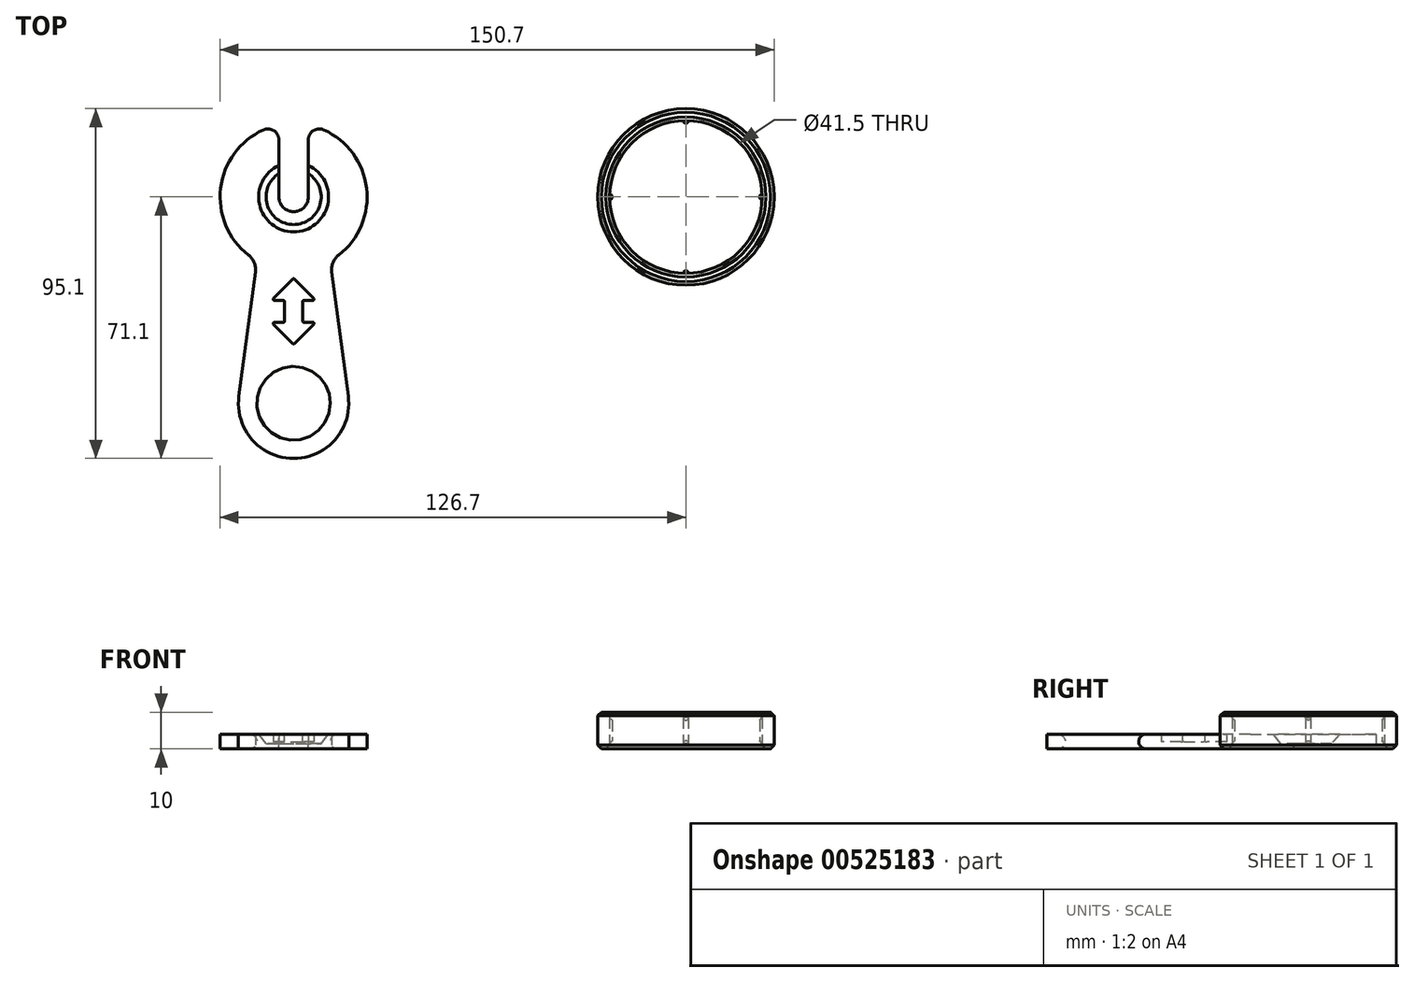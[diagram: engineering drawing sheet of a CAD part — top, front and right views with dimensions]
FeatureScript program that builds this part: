
annotation { "Feature Type Name" : "Feature", "Feature Type Description" : "" }
export const myFeature = defineFeature(function(context is Context, id is Id, definition is map)
    precondition{}
    {
        {
            assignVariable(context, id + "F0", {"name" : "SPACER_DEPTH", "anyValue" : 10 * mm});
        }
        {
            var Q0;
            Q0=qCreatedBy(makeId("Top.planeOp"),FACE);
            var sketch = newSketch(context, id + "F1", { "sketchPlane" : qUnion([Q0])});
            skCircle(sketch, "E0", {"center": v(0, 0) * mm, "radius": 20.75 * mm});
            skCircle(sketch, "E1.0", {"center": v(0, 0) * mm, "radius": 24 * mm});
            skSolve(sketch);
        }
        {
            var Q0;
            Q0=makeQuery(id+"F1.imprint","IMPRINT",FACE,{"disambiguationData":[TD([[makeQuery(id+"F1.imprint","IMPRINT",EDGE,{"derivedFrom":sQuery(id+"F1.wireOp",EDGE,"E0")}),-1.0]])]});
            extrude(context, id + "F2", {"entities" : qUnion([Q0]), "depth" : getVariable(context, 'SPACER_DEPTH'), "offsetDistance" : 25 * mm});
        }
        {
            var Q0;
            Q0=makeQuery(id+"F2.opExtrude","CAP_EDGE",EDGE,{"disambiguationData":[OSD([sQuery(id+"F1.wireOp",EDGE,"E0")])],"isStart":false});
            var Q1;
            Q1=makeQuery(id+"F2.opExtrude","CAP_EDGE",EDGE,{"disambiguationData":[OSD([sQuery(id+"F1.wireOp",EDGE,"E0")])],"isStart":true});
            var Q2;
            Q2=makeQuery(id+"F2.opExtrude","CAP_EDGE",EDGE,{"disambiguationData":[OSD([sQuery(id+"F1.wireOp",EDGE,"E1.0")])],"isStart":false});
            var Q3;
            Q3=makeQuery(id+"F2.opExtrude","CAP_EDGE",EDGE,{"disambiguationData":[OSD([sQuery(id+"F1.wireOp",EDGE,"E1.0")])],"isStart":true});
            chamfer(context, id + "F3", {"entities" : qUnion([Q0, Q1, Q2, Q3]), "width" : 1 * mm, "tangentPropagation" : true});
        }
        {
            var Q0;
            Q0=qCreatedBy(makeId("Top.planeOp"),FACE);
            cPlane(context, id + "F4", {"entities" : qUnion([Q0]), "cplaneType" : CPlaneType.OFFSET, "offset" : getVariable(context, 'SPACER_DEPTH') / 2, "width" : 150 * mm, "height" : 150 * mm});
        }
        {
            var Q0;
            Q0=qCreatedBy(id+"F4.planeOp",FACE);
            var sketch = newSketch(context, id + "F5", { "sketchPlane" : qUnion([Q0])});
            skCircle(sketch, "E2.0", {"center": v(0, 0) * mm, "radius": 20.75 * mm, "construction": true});
            skCircle(sketch, "E3", {"center": v(-20.75, 0) * mm, "radius": 0.7 * mm});
            skCircle(sketch, "E4.1.0", {"center": v(0, -20.75) * mm, "radius": 0.7 * mm});
            skCircle(sketch, "E4.2.0", {"center": v(20.75, 0) * mm, "radius": 0.7 * mm});
            skCircle(sketch, "E4.3.0", {"center": v(0, 20.75) * mm, "radius": 0.7 * mm});
            skSolve(sketch);
        }
        {
            var Q0;
            Q0 = qSketchRegion(id + "F5", true);
            extrude(context, id + "F6", {"entities" : qUnion([Q0]), "operationType" : NewBodyOperationType.ADD, "endBound" : BoundingType.SYMMETRIC, "depth" : getVariable(context, 'SPACER_DEPTH') / 2, "offsetDistance" : 25 * mm});
        }
        {
            var Q0;
            Q0=makeQuery(id+"F6.boolean.opBoolean","INTERSECT",EDGE,{"derivedFrom":[makeQuery(id+"F2.opExtrude","SWEPT_FACE",FACE,{"disambiguationData":[OSD([sQuery(id+"F1.wireOp",EDGE,"E0")])]}),makeQuery(id+"F6.opExtrude","CAP_FACE",FACE,{"disambiguationData":[OSD([sQuery(id+"F5.wireOp",EDGE,"E4.3.0")])],"isStart":false})]});
            var Q1;
            Q1=makeQuery(id+"F6.boolean.opBoolean","INTERSECT",EDGE,{"derivedFrom":[makeQuery(id+"F2.opExtrude","SWEPT_FACE",FACE,{"disambiguationData":[OSD([sQuery(id+"F1.wireOp",EDGE,"E0")])]}),makeQuery(id+"F6.opExtrude","CAP_FACE",FACE,{"disambiguationData":[OSD([sQuery(id+"F5.wireOp",EDGE,"E3")])],"isStart":false})]});
            var Q2;
            Q2=makeQuery(id+"F6.boolean.opBoolean","INTERSECT",EDGE,{"derivedFrom":[makeQuery(id+"F2.opExtrude","SWEPT_FACE",FACE,{"disambiguationData":[OSD([sQuery(id+"F1.wireOp",EDGE,"E0")])]}),makeQuery(id+"F6.opExtrude","CAP_FACE",FACE,{"disambiguationData":[OSD([sQuery(id+"F5.wireOp",EDGE,"E4.2.0")])],"isStart":false})]});
            var Q3;
            Q3=makeQuery(id+"F6.boolean.opBoolean","INTERSECT",EDGE,{"derivedFrom":[makeQuery(id+"F2.opExtrude","SWEPT_FACE",FACE,{"disambiguationData":[OSD([sQuery(id+"F1.wireOp",EDGE,"E0")])]}),makeQuery(id+"F6.opExtrude","CAP_FACE",FACE,{"disambiguationData":[OSD([sQuery(id+"F5.wireOp",EDGE,"E4.1.0")])],"isStart":false})]});
            var Q4;
            Q4=makeQuery(id+"F6.boolean.opBoolean","INTERSECT",EDGE,{"derivedFrom":[makeQuery(id+"F2.opExtrude","SWEPT_FACE",FACE,{"disambiguationData":[OSD([sQuery(id+"F1.wireOp",EDGE,"E0")])]}),makeQuery(id+"F6.opExtrude","CAP_FACE",FACE,{"disambiguationData":[OSD([sQuery(id+"F5.wireOp",EDGE,"E4.3.0")])],"isStart":true})]});
            var Q5;
            Q5=makeQuery(id+"F6.boolean.opBoolean","INTERSECT",EDGE,{"derivedFrom":[makeQuery(id+"F2.opExtrude","SWEPT_FACE",FACE,{"disambiguationData":[OSD([sQuery(id+"F1.wireOp",EDGE,"E0")])]}),makeQuery(id+"F6.opExtrude","CAP_FACE",FACE,{"disambiguationData":[OSD([sQuery(id+"F5.wireOp",EDGE,"E4.2.0")])],"isStart":true})]});
            var Q6;
            Q6=makeQuery(id+"F6.boolean.opBoolean","INTERSECT",EDGE,{"derivedFrom":[makeQuery(id+"F2.opExtrude","SWEPT_FACE",FACE,{"disambiguationData":[OSD([sQuery(id+"F1.wireOp",EDGE,"E0")])]}),makeQuery(id+"F6.opExtrude","CAP_FACE",FACE,{"disambiguationData":[OSD([sQuery(id+"F5.wireOp",EDGE,"E4.1.0")])],"isStart":true})]});
            var Q7;
            Q7=makeQuery(id+"F6.boolean.opBoolean","INTERSECT",EDGE,{"derivedFrom":[makeQuery(id+"F2.opExtrude","SWEPT_FACE",FACE,{"disambiguationData":[OSD([sQuery(id+"F1.wireOp",EDGE,"E0")])]}),makeQuery(id+"F6.opExtrude","CAP_FACE",FACE,{"disambiguationData":[OSD([sQuery(id+"F5.wireOp",EDGE,"E3")])],"isStart":true})]});
            chamfer(context, id + "F7", {"entities" : qUnion([Q0, Q1, Q2, Q3, Q4, Q5, Q6, Q7]), "width" : 1 * mm, "tangentPropagation" : true});
        }
        {
            var Q0;
            Q0=qCreatedBy(makeId("Top.planeOp"),FACE);
            var sketch = newSketch(context, id + "F8", { "sketchPlane" : qUnion([Q0])});
            skCircle(sketch, "E5", {"center": v(-106.7, 0) * mm, "radius": 4 * mm});
            skCircle(sketch, "E6", {"center": v(-106.7, 0) * mm, "radius": 20 * mm});
            skCircle(sketch, "E7", {"center": v(-106.7, -56.1) * mm, "radius": 15 * mm});
            skLineSegment(sketch, "E8", {"start": v(-106.7, 31.77) * mm, "end": v(-106.7, -83.91) * mm, "construction": true});
            skLineSegment(sketch, "E9", {"start": v(-116.7, -17.32) * mm, "end": v(-121.57, -54.13) * mm});
            skLineSegment(sketch, "E10", {"start": v(-96.7, -17.32) * mm, "end": v(-91.83, -54.13) * mm});
            skCircle(sketch, "E11.0", {"center": v(-106.7, -56.1) * mm, "radius": 10 * mm});
            skSolve(sketch);
        }
        {
            var Q0;
            {var subQ0=sQuery(id+"F8.wireOp",EDGE,"tMZcsfvI-P9a6-IfvE-EsAQ-RMbjLVvdxzLP");var subQ1=sQuery(id+"F8.wireOp",EDGE,"E5");var subQ2=makeQuery(id+"F8.imprint","INTERSECT",VERTEX,{"disambiguationData":[OD(0.0)],"derivedFrom":[subQ1,subQ0]});Q0=makeQuery(id+"F8.imprint","IMPRINT",FACE,{"disambiguationData":[TD([[makeQuery(id+"F8.imprint","IMPRINT",EDGE,{"disambiguationData":[TD([[subQ2,-1.0]])],"derivedFrom":subQ1}),-1.0]])]});}
            var Q1;
            {var subQ0=sQuery(id+"F8.wireOp",EDGE,"tMZcsfvI-P9a6-IfvE-EsAQ-RMbjLVvdxzLP");var subQ1=sQuery(id+"F8.wireOp",EDGE,"E5");var subQ2=makeQuery(id+"F8.imprint","INTERSECT",VERTEX,{"disambiguationData":[OD(0.0)],"derivedFrom":[subQ1,subQ0]});Q1=makeQuery(id+"F8.imprint","IMPRINT",FACE,{"disambiguationData":[TD([[makeQuery(id+"F8.imprint","IMPRINT",EDGE,{"disambiguationData":[TD([[subQ2,1.0]])],"derivedFrom":subQ1}),-1.0]])]});}
            var Q2;
            {var subQ0=sQuery(id+"F8.wireOp",EDGE,"d99b7d63-3b80-4857-949c-220825ab7e3a.1.0");var subQ1=sQuery(id+"F8.wireOp",EDGE,"E5");var subQ2=makeQuery(id+"F8.imprint","INTERSECT",VERTEX,{"disambiguationData":[OD(0.0)],"derivedFrom":[subQ1,subQ0]});Q2=makeQuery(id+"F8.imprint","IMPRINT",FACE,{"disambiguationData":[TD([[makeQuery(id+"F8.imprint","IMPRINT",EDGE,{"disambiguationData":[TD([[subQ2,1.0]])],"derivedFrom":subQ1}),-1.0]])]});}
            var Q3;
            {var subQ0=sQuery(id+"F8.wireOp",EDGE,"tMZcsfvI-P9a6-IfvE-EsAQ-RMbjLVvdxzLP");var subQ1=sQuery(id+"F8.wireOp",EDGE,"E5");var subQ2=makeQuery(id+"F8.imprint","INTERSECT",VERTEX,{"disambiguationData":[OD(1.0)],"derivedFrom":[subQ1,subQ0]});Q3=makeQuery(id+"F8.imprint","IMPRINT",FACE,{"disambiguationData":[TD([[makeQuery(id+"F8.imprint","IMPRINT",EDGE,{"disambiguationData":[TD([[subQ2,-1.0]])],"derivedFrom":subQ1}),-1.0]])]});}
            var Q4;
            {var subQ0=sQuery(id+"F8.wireOp",EDGE,"d99b7d63-3b80-4857-949c-220825ab7e3a.1.0");var subQ1=sQuery(id+"F8.wireOp",EDGE,"E5");var subQ2=makeQuery(id+"F8.imprint","INTERSECT",VERTEX,{"disambiguationData":[OD(1.0)],"derivedFrom":[subQ1,subQ0]});Q4=makeQuery(id+"F8.imprint","IMPRINT",FACE,{"disambiguationData":[TD([[makeQuery(id+"F8.imprint","IMPRINT",EDGE,{"disambiguationData":[TD([[subQ2,-1.0]])],"derivedFrom":subQ1}),-1.0]])]});}
            var Q5;
            {var subQ0=sQuery(id+"F8.wireOp",EDGE,"d99b7d63-3b80-4857-949c-220825ab7e3a.2.0");var subQ1=sQuery(id+"F8.wireOp",EDGE,"E5");var subQ2=makeQuery(id+"F8.imprint","INTERSECT",VERTEX,{"disambiguationData":[OD(0.0)],"derivedFrom":[subQ1,subQ0]});Q5=makeQuery(id+"F8.imprint","IMPRINT",FACE,{"disambiguationData":[TD([[makeQuery(id+"F8.imprint","IMPRINT",EDGE,{"disambiguationData":[TD([[subQ2,-1.0]])],"derivedFrom":subQ1}),-1.0]])]});}
            var Q6;
            {var subQ0=sQuery(id+"F8.wireOp",EDGE,"tMZcsfvI-P9a6-IfvE-EsAQ-RMbjLVvdxzLP");var subQ2=sQuery(id+"F8.wireOp",EDGE,"E6");var subQ3=makeQuery(id+"F8.imprint","INTERSECT",VERTEX,{"disambiguationData":[OD(0.0)],"derivedFrom":[subQ2,subQ0]});Q6=makeQuery(id+"F8.imprint","IMPRINT",FACE,{"disambiguationData":[TD([[makeQuery(id+"F8.imprint","IMPRINT",EDGE,{"disambiguationData":[TD([[subQ3,1.0]])],"derivedFrom":subQ2}),-1.0]])]});}
            var Q7;
            {var subQ3=sQuery(id+"F8.wireOp",EDGE,"Im5QKdEk-1Ov4-L05K-2sT1-LfVvJZR5fO0I");Q7=makeQuery(id+"F8.imprint","IMPRINT",FACE,{"disambiguationData":[TD([[makeQuery(id+"F8.imprint","IMPRINT",EDGE,{"derivedFrom":subQ3}),-1.0]])]});}
            var Q8;
            {var subQ3=sQuery(id+"F8.wireOp",EDGE,"e6c83034-2231-4307-ba1c-9a527880b54f0.MirrorCS");Q8=makeQuery(id+"F8.imprint","IMPRINT",FACE,{"disambiguationData":[TD([[makeQuery(id+"F8.imprint","IMPRINT",EDGE,{"derivedFrom":subQ3}),1.0]])]});}
            var Q9;
            {var subQ3=sQuery(id+"F8.wireOp",EDGE,"7b8f1f18-21e0-4d82-9494-f1d715cf9ae4.2.0");Q9=makeQuery(id+"F8.imprint","IMPRINT",FACE,{"disambiguationData":[TD([[makeQuery(id+"F8.imprint","IMPRINT",EDGE,{"derivedFrom":subQ3}),-1.0]])]});}
            var Q10;
            {var subQ0=sQuery(id+"F8.wireOp",EDGE,"tMZcsfvI-P9a6-IfvE-EsAQ-RMbjLVvdxzLP");var subQ6=sQuery(id+"F8.wireOp",EDGE,"E6");var subQ7=makeQuery(id+"F8.imprint","INTERSECT",VERTEX,{"disambiguationData":[OD(1.0)],"derivedFrom":[subQ6,subQ0]});Q10=makeQuery(id+"F8.imprint","IMPRINT",FACE,{"disambiguationData":[TD([[makeQuery(id+"F8.imprint","IMPRINT",EDGE,{"disambiguationData":[TD([[subQ7,-1.0]])],"derivedFrom":subQ6}),-1.0]])]});}
            var Q11;
            {var subQ3=sQuery(id+"F8.wireOp",EDGE,"92c590d0-b01e-4f62-b96a-7e57a4e76e70.2.0");Q11=makeQuery(id+"F8.imprint","IMPRINT",FACE,{"disambiguationData":[TD([[makeQuery(id+"F8.imprint","IMPRINT",EDGE,{"derivedFrom":subQ3}),1.0]])]});}
            var Q12;
            {var subQ3=sQuery(id+"F8.wireOp",EDGE,"7b8f1f18-21e0-4d82-9494-f1d715cf9ae4.1.0");Q12=makeQuery(id+"F8.imprint","IMPRINT",FACE,{"disambiguationData":[TD([[makeQuery(id+"F8.imprint","IMPRINT",EDGE,{"derivedFrom":subQ3}),-1.0]])]});}
            var Q13;
            {var subQ4=sQuery(id+"F8.wireOp",EDGE,"d99b7d63-3b80-4857-949c-220825ab7e3a.2.0");var subQ6=sQuery(id+"F8.wireOp",EDGE,"E6");var subQ8=makeQuery(id+"F8.imprint","INTERSECT",VERTEX,{"disambiguationData":[OD(0.0)],"derivedFrom":[subQ6,subQ4]});Q13=makeQuery(id+"F8.imprint","IMPRINT",FACE,{"disambiguationData":[TD([[makeQuery(id+"F8.imprint","IMPRINT",EDGE,{"disambiguationData":[TD([[subQ8,-1.0]])],"derivedFrom":subQ6}),-1.0]])]});}
            var Q14;
            {var subQ3=sQuery(id+"F8.wireOp",EDGE,"92c590d0-b01e-4f62-b96a-7e57a4e76e70.1.0");Q14=makeQuery(id+"F8.imprint","IMPRINT",FACE,{"disambiguationData":[TD([[makeQuery(id+"F8.imprint","IMPRINT",EDGE,{"derivedFrom":subQ3}),1.0]])]});}
            var Q15;
            Q15=makeQuery(id+"F8.imprint","IMPRINT",FACE,{"disambiguationData":[TD([[makeQuery(id+"F8.imprint","IMPRINT",EDGE,{"derivedFrom":sQuery(id+"F8.wireOp",EDGE,"E11.0")}),-1.0]])]});
            extrude(context, id + "F9", {"entities" : qUnion([Q0, Q1, Q2, Q3, Q4, Q5, Q6, Q7, Q8, Q9, Q10, Q11, Q12, Q13, Q14, Q15]), "depth" : 4 * mm, "offsetDistance" : 25 * mm});
        }
        {
            var Q0;
            Q0=makeQuery(id+"F9.opExtrude","CAP_FACE",FACE,{"disambiguationData":[OSD([sQuery(id+"F8.wireOp",EDGE,"E5"),sQuery(id+"F8.wireOp",EDGE,"E6"),sQuery(id+"F8.wireOp",EDGE,"JQelNSBS-weLF-Z4lI-uK8G-V99NbtTbeSVU"),sQuery(id+"F8.wireOp",EDGE,"tMZcsfvI-P9a6-IfvE-EsAQ-RMbjLVvdxzLP"),sQuery(id+"F8.wireOp",EDGE,"d99b7d63-3b80-4857-949c-220825ab7e3a.1.0"),sQuery(id+"F8.wireOp",EDGE,"d99b7d63-3b80-4857-949c-220825ab7e3a.2.0"),sQuery(id+"F8.wireOp",EDGE,"Im5QKdEk-1Ov4-L05K-2sT1-LfVvJZR5fO0I"),sQuery(id+"F8.wireOp",EDGE,"7b8f1f18-21e0-4d82-9494-f1d715cf9ae4.1.0"),sQuery(id+"F8.wireOp",EDGE,"7b8f1f18-21e0-4d82-9494-f1d715cf9ae4.2.0"),sQuery(id+"F8.wireOp",EDGE,"e6c83034-2231-4307-ba1c-9a527880b54f0.MirrorCS"),sQuery(id+"F8.wireOp",EDGE,"92c590d0-b01e-4f62-b96a-7e57a4e76e70.1.0"),sQuery(id+"F8.wireOp",EDGE,"92c590d0-b01e-4f62-b96a-7e57a4e76e70.2.0")])],"isStart":false});
            var sketch = newSketch(context, id + "F10", { "sketchPlane" : qUnion([Q0])});
            skCircle(sketch, "E12.0", {"center": v(-106.7, 0) * mm, "radius": 4 * mm, "construction": true});
            skCircle(sketch, "E13", {"center": v(-106.7, 0) * mm, "radius": 9.5 * mm});
            skSolve(sketch);
        }
        {
            var Q0;
            Q0=makeQuery(id+"F10.imprint","IMPRINT",FACE,{"disambiguationData":[TD([[makeQuery(id+"F10.imprint","IMPRINT",EDGE,{"derivedFrom":sQuery(id+"F10.wireOp",EDGE,"E13")}),1.0]])]});
            extrude(context, id + "F11", {"entities" : qUnion([Q0]), "operationType" : NewBodyOperationType.REMOVE, "oppositeDirection" : true, "depth" : 2.5 * mm, "offsetDistance" : 25 * mm});
        }
        {
            var Q0;
            Q0=makeQuery(id+"F11.boolean.opBoolean","COPY",EDGE,{"derivedFrom":makeQuery(id+"F11.opExtrude","CAP_EDGE",EDGE,{"disambiguationData":[OSD([sQuery(id+"F10.wireOp",EDGE,"E13")])],"isStart":false})});
            chamfer(context, id + "F12", {"entities" : qUnion([Q0]), "chamferType" : ChamferType.TWO_OFFSETS, "width1" : 2 * mm, "oppositeDirection" : false, "width2" : 2.5 * mm, "tangentPropagation" : true});
        }
        {
            var Q0;
            Q0=makeQuery(id+"F9.opExtrude","CAP_FACE",FACE,{"disambiguationData":[OSD([sQuery(id+"F8.wireOp",EDGE,"E5"),sQuery(id+"F8.wireOp",EDGE,"E6"),sQuery(id+"F8.wireOp",EDGE,"E7"),sQuery(id+"F8.wireOp",EDGE,"E9"),sQuery(id+"F8.wireOp",EDGE,"E10"),sQuery(id+"F8.wireOp",EDGE,"E11.0")])],"isStart":false});
            var sketch = newSketch(context, id + "F13", { "sketchPlane" : qUnion([Q0])});
            skLineSegment(sketch, "E14.0", {"start": v(-106.7, 31.77) * mm, "end": v(-106.7, -83.91) * mm, "construction": true});
            skCircle(sketch, "E15.0", {"center": v(-106.7, 0) * mm, "radius": 4 * mm});
            skLineSegment(sketch, "E16", {"start": v(-110.7, 0) * mm, "end": v(-110.7, 21) * mm});
            skLineSegment(sketch, "E17", {"start": v(-102.7, 0) * mm, "end": v(-102.7, 21) * mm});
            skPoint(sketch, "E18", {"position": v(-106.7, 20) * mm});
            skLineSegment(sketch, "E19", {"start": v(-110.7, 21) * mm, "end": v(-102.7, 21) * mm});
            skSolve(sketch);
        }
        {
            var Q0;
            {var subQ0=sQuery(id+"F13.wireOp",EDGE,"E19");Q0=makeQuery(id+"F13.imprint","IMPRINT",FACE,{"disambiguationData":[TD([[makeQuery(id+"F13.imprint","IMPRINT",EDGE,{"derivedFrom":subQ0}),-1.0]])]});}
            var Q1;
            {var subQ0=sQuery(id+"F13.wireOp",EDGE,"E16");var subQ1=sQuery(id+"F8.wireOp",EDGE,"E6");var subQ2=makeQuery(id+"F9.opExtrude","CAP_EDGE",EDGE,{"disambiguationData":[OSD([subQ1])],"isStart":false});var subQ3=makeQuery(id+"F13.imprint","INTERSECT",VERTEX,{"derivedFrom":[subQ2,subQ0]});Q1=makeQuery(id+"F13.imprint","IMPRINT",FACE,{"disambiguationData":[TD([[makeQuery(id+"F13.imprint","IMPRINT",EDGE,{"disambiguationData":[TD([[subQ3,1.0]])],"derivedFrom":subQ2}),1.0]])]});}
            var Q2;
            {var subQ0=sQuery(id+"F13.wireOp",EDGE,"E16");var subQ1=sQuery(id+"F13.wireOp",EDGE,"E15.0");var subQ2=makeQuery(id+"F13.imprint","INTERSECT",VERTEX,{"derivedFrom":[subQ1,subQ0]});Q2=makeQuery(id+"F13.imprint","IMPRINT",FACE,{"disambiguationData":[TD([[makeQuery(id+"F13.imprint","IMPRINT",EDGE,{"disambiguationData":[TD([[subQ2,1.0]])],"derivedFrom":subQ1}),-1.0]])]});}
            extrude(context, id + "F14", {"entities" : qUnion([Q0, Q1, Q2]), "operationType" : NewBodyOperationType.REMOVE, "endBound" : BoundingType.THROUGH_ALL, "oppositeDirection" : true, "depth" : 25 * mm, "offsetDistance" : 25 * mm});
        }
        {
            var Q0;
            Q0=makeQuery(id+"F14.boolean.opBoolean","INTERSECT",EDGE,{"derivedFrom":[makeQuery(id+"F9.opExtrude","SWEPT_FACE",FACE,{"disambiguationData":[OSD([sQuery(id+"F8.wireOp",EDGE,"E6")])]}),makeQuery(id+"F14.opExtrude","SWEPT_FACE",FACE,{"disambiguationData":[OSD([sQuery(id+"F13.wireOp",EDGE,"E16")])]})]});
            var Q1;
            Q1=makeQuery(id+"F14.boolean.opBoolean","INTERSECT",EDGE,{"derivedFrom":[makeQuery(id+"F9.opExtrude","SWEPT_FACE",FACE,{"disambiguationData":[OSD([sQuery(id+"F8.wireOp",EDGE,"E6")])]}),makeQuery(id+"F14.opExtrude","SWEPT_FACE",FACE,{"disambiguationData":[OSD([sQuery(id+"F13.wireOp",EDGE,"E17")])]})]});
            fillet(context, id + "F15", {"entities" : qUnion([Q0, Q1]), "radius" : 3 * mm, "tangentPropagation" : true, "allowEdgeOverflow" : false});
        }
        {
            var Q0;
            Q0=makeQuery(id+"F9.opExtrude","SWEPT_EDGE",EDGE,{"disambiguationData":[OSD([sQuery(id+"F8.wireOp",EDGE,"E6"),sQuery(id+"F8.wireOp",EDGE,"E10")])]});
            var Q1;
            Q1=makeQuery(id+"F9.opExtrude","SWEPT_EDGE",EDGE,{"disambiguationData":[OSD([sQuery(id+"F8.wireOp",EDGE,"E6"),sQuery(id+"F8.wireOp",EDGE,"E9")])]});
            fillet(context, id + "F16", {"entities" : qUnion([Q0, Q1]), "radius" : 5 * mm, "tangentPropagation" : true, "allowEdgeOverflow" : false});
        }
        {
            var Q0;
            Q0=makeQuery(id+"F9.opExtrude","CAP_EDGE",EDGE,{"disambiguationData":[OSD([sQuery(id+"F8.wireOp",EDGE,"E11.0")])],"isStart":false});
            var Q1;
            Q1=makeQuery(id+"F9.opExtrude","CAP_EDGE",EDGE,{"disambiguationData":[OSD([sQuery(id+"F8.wireOp",EDGE,"E11.0")])],"isStart":true});
            fillet(context, id + "F17", {"entities" : qUnion([Q0, Q1]), "radius" : 2 * mm, "tangentPropagation" : true, "allowEdgeOverflow" : false});
        }
        {
            var Q0;
            Q0=makeQuery(id+"F9.opExtrude","CAP_FACE",FACE,{"disambiguationData":[OSD([sQuery(id+"F8.wireOp",EDGE,"E5"),sQuery(id+"F8.wireOp",EDGE,"E6"),sQuery(id+"F8.wireOp",EDGE,"E7"),sQuery(id+"F8.wireOp",EDGE,"E9"),sQuery(id+"F8.wireOp",EDGE,"E10"),sQuery(id+"F8.wireOp",EDGE,"E11.0")])],"isStart":false});
            var sketch = newSketch(context, id + "F18", { "sketchPlane" : qUnion([Q0])});
            skLineSegment(sketch, "E20.0", {"start": v(-106.7, 31.77) * mm, "end": v(-106.7, -83.91) * mm, "construction": true});
            skLineSegment(sketch, "E21", {"start": v(-109.2, -31.1) * mm, "end": v(-109.2, -34.1) * mm});
            skLineSegment(sketch, "E22", {"start": v(-109.2, -34.1) * mm, "end": v(-112.7, -34.1) * mm});
            skLineSegment(sketch, "E23", {"start": v(-112.7, -34.1) * mm, "end": v(-106.7, -40.1) * mm});
            skLineSegment(sketch, "E24", {"start": v(-106.7, -40.1) * mm, "end": v(-100.7, -34.1) * mm});
            skLineSegment(sketch, "E25", {"start": v(-100.7, -34.1) * mm, "end": v(-104.2, -34.1) * mm});
            skLineSegment(sketch, "E26", {"start": v(-104.2, -34.1) * mm, "end": v(-104.2, -31.1) * mm});
            skLineSegment(sketch, "E27", {"start": v(-109.2, -31.1) * mm, "end": v(-104.2, -31.1) * mm, "construction": true});
            skLineSegment(sketch, "E28.MirrorCS", {"start": v(-109.2, -31.1) * mm, "end": v(-109.2, -28.1) * mm});
            skLineSegment(sketch, "E29.MirrorCS", {"start": v(-109.2, -28.1) * mm, "end": v(-112.7, -28.1) * mm});
            skLineSegment(sketch, "E30.MirrorCS", {"start": v(-112.7, -28.1) * mm, "end": v(-106.7, -22.1) * mm});
            skLineSegment(sketch, "E31.MirrorCS", {"start": v(-106.7, -22.1) * mm, "end": v(-100.7, -28.1) * mm});
            skLineSegment(sketch, "E32.MirrorCS", {"start": v(-100.7, -28.1) * mm, "end": v(-104.2, -28.1) * mm});
            skLineSegment(sketch, "E33.MirrorCS", {"start": v(-104.2, -28.1) * mm, "end": v(-104.2, -31.1) * mm});
            skCircle(sketch, "E34.1", {"center": v(-106.7, -56.1) * mm, "radius": 12 * mm, "construction": true});
            skPoint(sketch, "E35", {"position": v(-106.7, -44.1) * mm});
            skSolve(sketch);
        }
        {
            var Q0;
            Q0 = qSketchRegion(id + "F18", true);
            extrude(context, id + "F19", {"entities" : qUnion([Q0]), "operationType" : NewBodyOperationType.REMOVE, "oppositeDirection" : true, "depth" : 2 * mm, "offsetDistance" : 25 * mm});
        }
        {
            var Q0;
            Q0=makeQuery(id+"F19.boolean.opBoolean","COPY",EDGE,{"derivedFrom":makeQuery(id+"F19.opExtrude","SWEPT_EDGE",EDGE,{"disambiguationData":[OSD([sQuery(id+"F18.wireOp",EDGE,"E29.MirrorCS"),sQuery(id+"F18.wireOp",EDGE,"E30.MirrorCS")])]})});
            var Q1;
            Q1=makeQuery(id+"F19.boolean.opBoolean","COPY",EDGE,{"derivedFrom":makeQuery(id+"F19.opExtrude","SWEPT_EDGE",EDGE,{"disambiguationData":[OSD([sQuery(id+"F18.wireOp",EDGE,"E31.MirrorCS"),sQuery(id+"F18.wireOp",EDGE,"E32.MirrorCS")])]})});
            var Q2;
            Q2=makeQuery(id+"F19.boolean.opBoolean","COPY",EDGE,{"derivedFrom":makeQuery(id+"F19.opExtrude","SWEPT_EDGE",EDGE,{"disambiguationData":[OSD([sQuery(id+"F18.wireOp",EDGE,"E24"),sQuery(id+"F18.wireOp",EDGE,"E25")])]})});
            var Q3;
            Q3=makeQuery(id+"F19.boolean.opBoolean","COPY",EDGE,{"derivedFrom":makeQuery(id+"F19.opExtrude","SWEPT_EDGE",EDGE,{"disambiguationData":[OSD([sQuery(id+"F18.wireOp",EDGE,"E22"),sQuery(id+"F18.wireOp",EDGE,"E23")])]})});
            var Q4;
            Q4=makeQuery(id+"F19.boolean.opBoolean","COPY",EDGE,{"derivedFrom":makeQuery(id+"F19.opExtrude","SWEPT_EDGE",EDGE,{"disambiguationData":[OSD([sQuery(id+"F18.wireOp",EDGE,"E21"),sQuery(id+"F18.wireOp",EDGE,"E22")])]})});
            var Q5;
            Q5=makeQuery(id+"F19.boolean.opBoolean","COPY",EDGE,{"derivedFrom":makeQuery(id+"F19.opExtrude","SWEPT_EDGE",EDGE,{"disambiguationData":[OSD([sQuery(id+"F18.wireOp",EDGE,"E28.MirrorCS"),sQuery(id+"F18.wireOp",EDGE,"E29.MirrorCS")])]})});
            var Q6;
            Q6=makeQuery(id+"F19.boolean.opBoolean","COPY",EDGE,{"derivedFrom":makeQuery(id+"F19.opExtrude","SWEPT_EDGE",EDGE,{"disambiguationData":[OSD([sQuery(id+"F18.wireOp",EDGE,"E32.MirrorCS"),sQuery(id+"F18.wireOp",EDGE,"E33.MirrorCS")])]})});
            var Q7;
            Q7=makeQuery(id+"F19.boolean.opBoolean","COPY",EDGE,{"derivedFrom":makeQuery(id+"F19.opExtrude","SWEPT_EDGE",EDGE,{"disambiguationData":[OSD([sQuery(id+"F18.wireOp",EDGE,"E25"),sQuery(id+"F18.wireOp",EDGE,"E26")])]})});
            var Q8;
            Q8=makeQuery(id+"F19.boolean.opBoolean","COPY",EDGE,{"derivedFrom":makeQuery(id+"F19.opExtrude","SWEPT_EDGE",EDGE,{"disambiguationData":[OSD([sQuery(id+"F18.wireOp",EDGE,"E30.MirrorCS"),sQuery(id+"F18.wireOp",EDGE,"E31.MirrorCS")])]})});
            var Q9;
            Q9=makeQuery(id+"F19.boolean.opBoolean","COPY",EDGE,{"derivedFrom":makeQuery(id+"F19.opExtrude","SWEPT_EDGE",EDGE,{"disambiguationData":[OSD([sQuery(id+"F18.wireOp",EDGE,"E23"),sQuery(id+"F18.wireOp",EDGE,"E24")])]})});
            fillet(context, id + "F20", {"entities" : qUnion([Q0, Q1, Q2, Q3, Q4, Q5, Q6, Q7, Q8, Q9]), "radius" : 0.3 * mm, "tangentPropagation" : true, "allowEdgeOverflow" : false});
        }
    });
